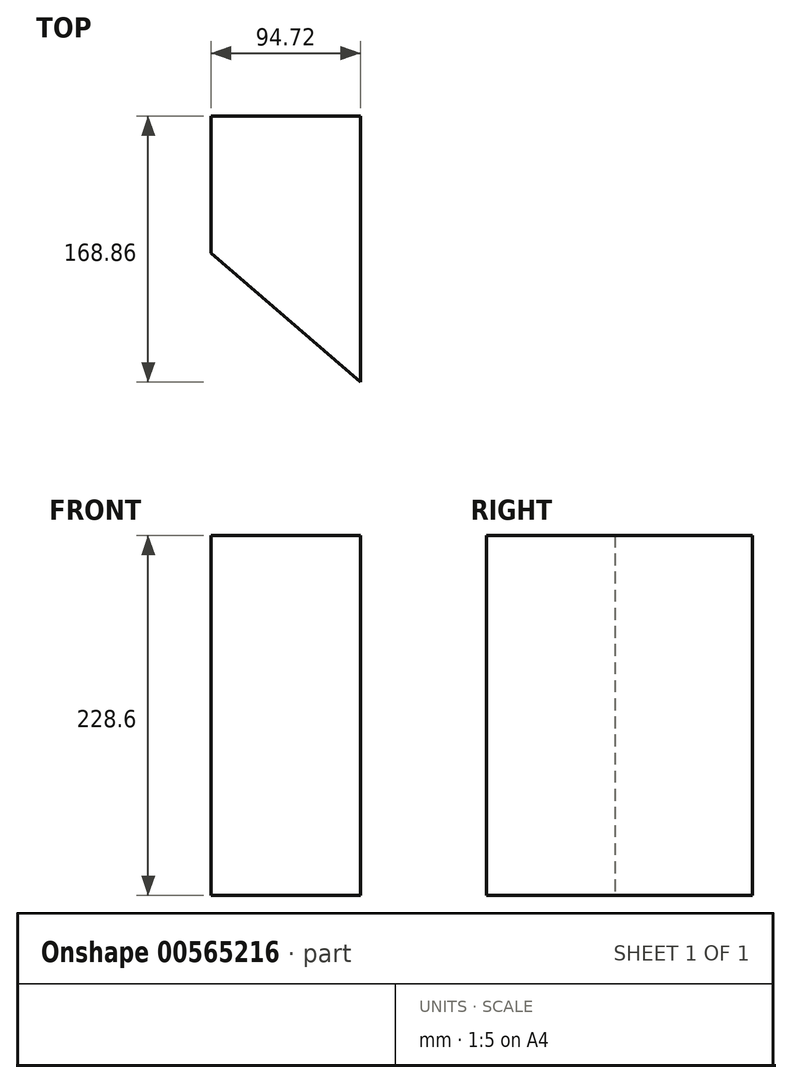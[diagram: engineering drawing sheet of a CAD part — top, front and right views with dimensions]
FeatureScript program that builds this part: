
annotation { "Feature Type Name" : "Feature", "Feature Type Description" : "" }
export const myFeature = defineFeature(function(context is Context, id is Id, definition is map)
    precondition{}
    {
        {
            var Q0;
            Q0=qCreatedBy(makeId("Top.planeOp"),FACE);
            var sketch = newSketch(context, id + "F0", { "sketchPlane" : qUnion([Q0])});
            skLineSegment(sketch, "E0.bottom", {"start": v(94.72, 87.97) * mm, "end": v(-98, 87.97) * mm});
            skLineSegment(sketch, "E0.top", {"start": v(94.72, -83.04) * mm, "end": v(-98, -83.04) * mm});
            skLineSegment(sketch, "E0.left", {"start": v(94.72, 87.97) * mm, "end": v(94.72, -83.04) * mm});
            skLineSegment(sketch, "E0.right", {"start": v(-98, 87.97) * mm, "end": v(-98, -83.04) * mm});
            skSolve(sketch);
        }
        {
            var Q0;
            Q0=sQuery(id+"F0.wireOp",EDGE,"E0.right");
            var Q1;
            Q1=sQuery(id+"F0.wireOp",EDGE,"E0.left");
            var Q2;
            Q2=sQuery(id+"F0.wireOp",EDGE,"E0.top");
            var Q3;
            Q3=sQuery(id+"F0.wireOp",EDGE,"E0.bottom");
            extrude(context, id + "F1", {"bodyType" : ToolBodyType.SURFACE, "surfaceEntities" : qUnion([Q0, Q1, Q2, Q3]), "depth" : 203.2 * mm, "offsetDistance" : 25.4 * mm});
        }
        {
            var Q0;
            Q0=makeQuery(id+"F0.imprint","IMPRINT",FACE,{"disambiguationData":[TD([[makeQuery(id+"F0.imprint","IMPRINT",EDGE,{"derivedFrom":sQuery(id+"F0.wireOp",EDGE,"E0.bottom")}),1.0]])]});
            var sketch = newSketch(context, id + "F2", { "sketchPlane" : qUnion([Q0])});
            skLineSegment(sketch, "E1", {"start": v(0, 0) * mm, "end": v(95.73, -82.67) * mm});
            skLineSegment(sketch, "E2", {"start": v(95.73, -82.67) * mm, "end": v(95.73, 87.07) * mm});
            skLineSegment(sketch, "E3", {"start": v(95.73, 87.07) * mm, "end": v(0, 87.07) * mm});
            skLineSegment(sketch, "E4", {"start": v(0, 87.07) * mm, "end": v(0, 0) * mm});
            skSolve(sketch);
        }
        {
            var Q0;
            {var subQ0=sQuery(id+"F2.wireOp",EDGE,"E4");Q0=makeQuery(id+"F2.imprint","IMPRINT",FACE,{"disambiguationData":[TD([[makeQuery(id+"F2.imprint","IMPRINT",EDGE,{"derivedFrom":subQ0}),1.0]])]});}
            extrude(context, id + "F3", {"entities" : qUnion([Q0]), "depth" : 228.6 * mm, "offsetDistance" : 25.4 * mm});
        }
    });
